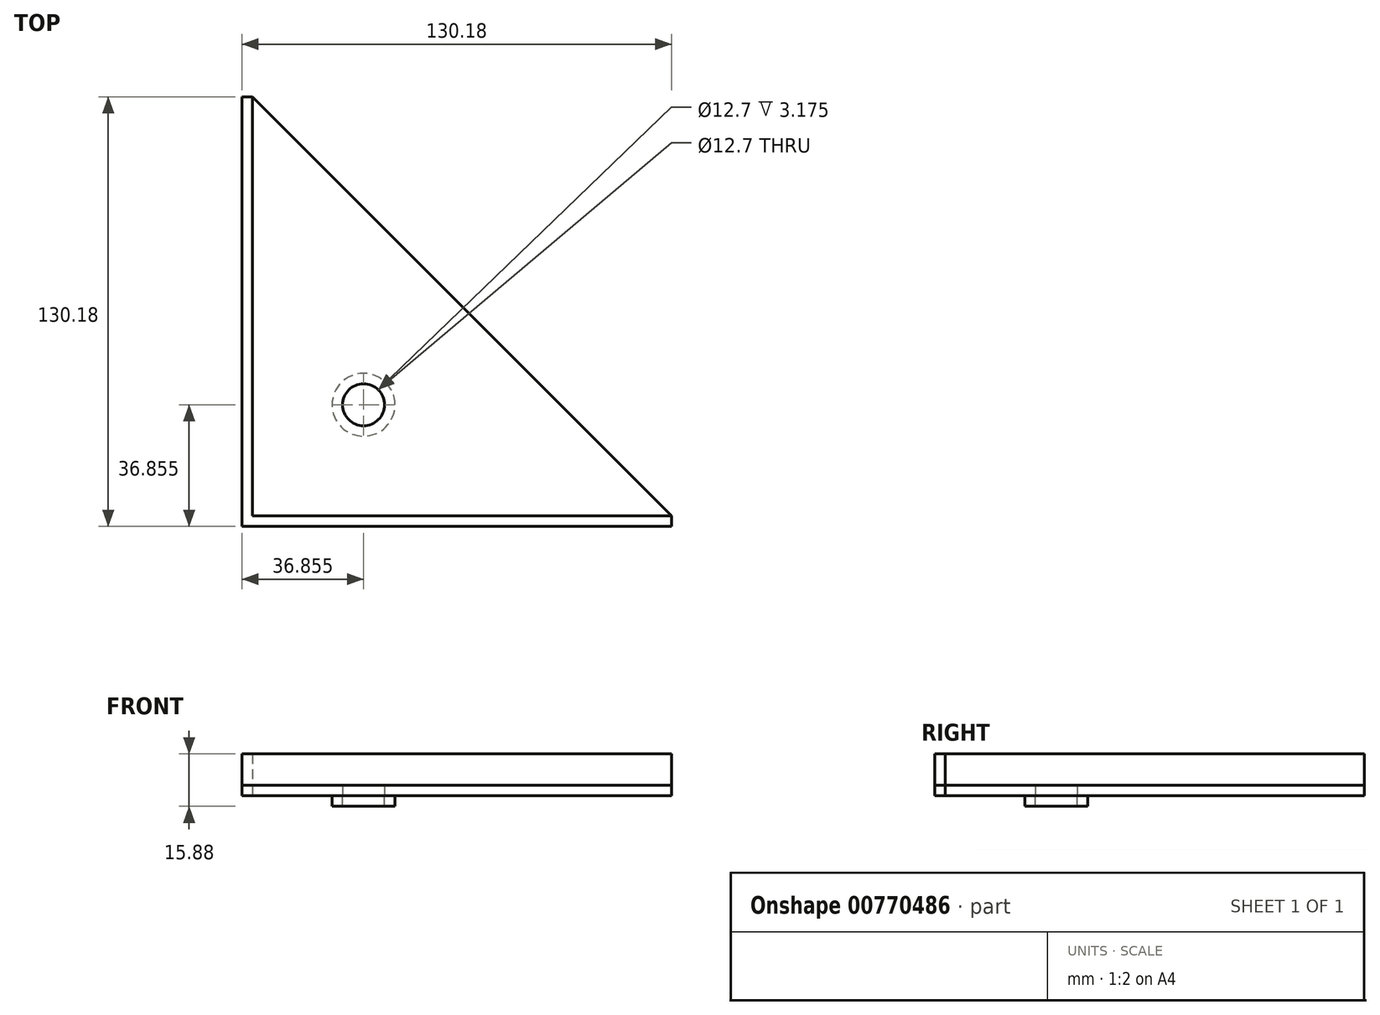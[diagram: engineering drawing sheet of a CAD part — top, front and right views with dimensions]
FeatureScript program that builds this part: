
annotation { "Feature Type Name" : "Feature", "Feature Type Description" : "" }
export const myFeature = defineFeature(function(context is Context, id is Id, definition is map)
    precondition{}
    {
        {
            var Q0;
            Q0=qCreatedBy(makeId("Top.planeOp"),FACE);
            var sketch = newSketch(context, id + "F0", { "sketchPlane" : qUnion([Q0])});
            skLineSegment(sketch, "E0", {"start": v(0, 0) * mm, "end": v(127, 0) * mm});
            skLineSegment(sketch, "E1", {"start": v(0, 0) * mm, "end": v(0, 127) * mm});
            skLineSegment(sketch, "E2.0", {"start": v(-3.17, -3.17) * mm, "end": v(-3.17, 127) * mm});
            skLineSegment(sketch, "E3.0", {"start": v(-3.17, -3.18) * mm, "end": v(127, -3.18) * mm});
            skLineSegment(sketch, "E4", {"start": v(127, -3.18) * mm, "end": v(127, 0) * mm});
            skLineSegment(sketch, "E5", {"start": v(0, 127) * mm, "end": v(-3.17, 127) * mm});
            skCircle(sketch, "E6", {"center": v(33.67, 33.67) * mm, "radius": 6.35 * mm});
            skLineSegment(sketch, "E7", {"start": v(127, 0) * mm, "end": v(0, 127) * mm});
            skCircle(sketch, "E8.0", {"center": v(33.67, 33.67) * mm, "radius": 9.53 * mm});
            skCircle(sketch, "E9", {"center": v(33.67, 33.67) * mm, "radius": 6.29 * mm});
            skLineSegment(sketch, "E10", {"start": v(33.67, 33.67) * mm, "end": v(8.57, 33.67) * mm, "construction": true});
            skLineSegment(sketch, "E11", {"start": v(33.67, 33.67) * mm, "end": v(33.67, 10.07) * mm, "construction": true});
            skSolve(sketch);
        }
        {
            var Q0;
            {var subQ9=sQuery(id+"F0.wireOp",EDGE,"E7");Q0=makeQuery(id+"F0.imprint","IMPRINT",FACE,{"disambiguationData":[TD([[makeQuery(id+"F0.imprint","IMPRINT",EDGE,{"derivedFrom":subQ9}),1.0]])]});}
            var Q1;
            {var subQ1=sQuery(id+"F0.wireOp",EDGE,"E0");var subQ5=sQuery(id+"F0.wireOp",EDGE,"E1");var subQ6=makeQuery(id+"F0.imprint","INTERSECT",VERTEX,{"derivedFrom":[subQ1,subQ5]});Q1=makeQuery(id+"F0.imprint","IMPRINT",FACE,{"disambiguationData":[TD([[makeQuery(id+"F0.imprint","IMPRINT",EDGE,{"disambiguationData":[TD([[subQ6,-1.0]])],"derivedFrom":subQ1}),1.0]])]});}
            var Q2;
            Q2=makeQuery(id+"F0.imprint","IMPRINT",FACE,{"disambiguationData":[TD([[makeQuery(id+"F0.imprint","IMPRINT",EDGE,{"derivedFrom":sQuery(id+"F0.wireOp",EDGE,"E2.0")}),-1.0]])]});
            var Q3;
            {var subQ0=sQuery(id+"F0.wireOp",EDGE,"cg00KGGl-9QHz-r3ZR-t2GE-rQK2B3L42RZA");var subQ1=sQuery(id+"F0.wireOp",EDGE,"E6");var subQ2=makeQuery(id+"F0.imprint","INTERSECT",VERTEX,{"derivedFrom":[subQ1,subQ0]});Q3=makeQuery(id+"F0.imprint","IMPRINT",FACE,{"disambiguationData":[TD([[makeQuery(id+"F0.imprint","IMPRINT",EDGE,{"disambiguationData":[TD([[subQ2,-1.0]])],"derivedFrom":subQ1}),-1.0]])]});}
            var Q4;
            {var subQ0=sQuery(id+"F0.wireOp",EDGE,"cg00KGGl-9QHz-r3ZR-t2GE-rQK2B3L42RZA");var subQ1=sQuery(id+"F0.wireOp",EDGE,"E6");var subQ2=makeQuery(id+"F0.imprint","INTERSECT",VERTEX,{"derivedFrom":[subQ1,subQ0]});Q4=makeQuery(id+"F0.imprint","IMPRINT",FACE,{"disambiguationData":[TD([[makeQuery(id+"F0.imprint","IMPRINT",EDGE,{"disambiguationData":[TD([[subQ2,1.0]])],"derivedFrom":subQ1}),-1.0]])]});}
            extrude(context, id + "F1", {"entities" : qUnion([Q0, Q1, Q2, Q3, Q4]), "depth" : 3.17 * mm, "offsetDistance" : 25.4 * mm});
        }
        {
            var Q0;
            Q0=makeQuery(id+"F0.imprint","IMPRINT",FACE,{"disambiguationData":[TD([[makeQuery(id+"F0.imprint","IMPRINT",EDGE,{"derivedFrom":sQuery(id+"F0.wireOp",EDGE,"E2.0")}),-1.0]])]});
            extrude(context, id + "F2", {"entities" : qUnion([Q0]), "depth" : 12.7 * mm, "offsetDistance" : 25.4 * mm});
        }
        {
            var Q0;
            {var subQ0=sQuery(id+"F0.wireOp",EDGE,"cg00KGGl-9QHz-r3ZR-t2GE-rQK2B3L42RZA");var subQ1=sQuery(id+"F0.wireOp",EDGE,"E6");var subQ2=makeQuery(id+"F0.imprint","INTERSECT",VERTEX,{"derivedFrom":[subQ1,subQ0]});Q0=makeQuery(id+"F0.imprint","IMPRINT",FACE,{"disambiguationData":[TD([[makeQuery(id+"F0.imprint","IMPRINT",EDGE,{"disambiguationData":[TD([[subQ2,-1.0]])],"derivedFrom":subQ1}),-1.0]])]});}
            var Q1;
            {var subQ0=sQuery(id+"F0.wireOp",EDGE,"cg00KGGl-9QHz-r3ZR-t2GE-rQK2B3L42RZA");var subQ1=sQuery(id+"F0.wireOp",EDGE,"E6");var subQ2=makeQuery(id+"F0.imprint","INTERSECT",VERTEX,{"derivedFrom":[subQ1,subQ0]});Q1=makeQuery(id+"F0.imprint","IMPRINT",FACE,{"disambiguationData":[TD([[makeQuery(id+"F0.imprint","IMPRINT",EDGE,{"disambiguationData":[TD([[subQ2,1.0]])],"derivedFrom":subQ1}),-1.0]])]});}
            extrude(context, id + "F3", {"entities" : qUnion([Q0, Q1]), "oppositeDirection" : true, "depth" : 3.17 * mm, "offsetDistance" : 25.4 * mm});
        }
    });
